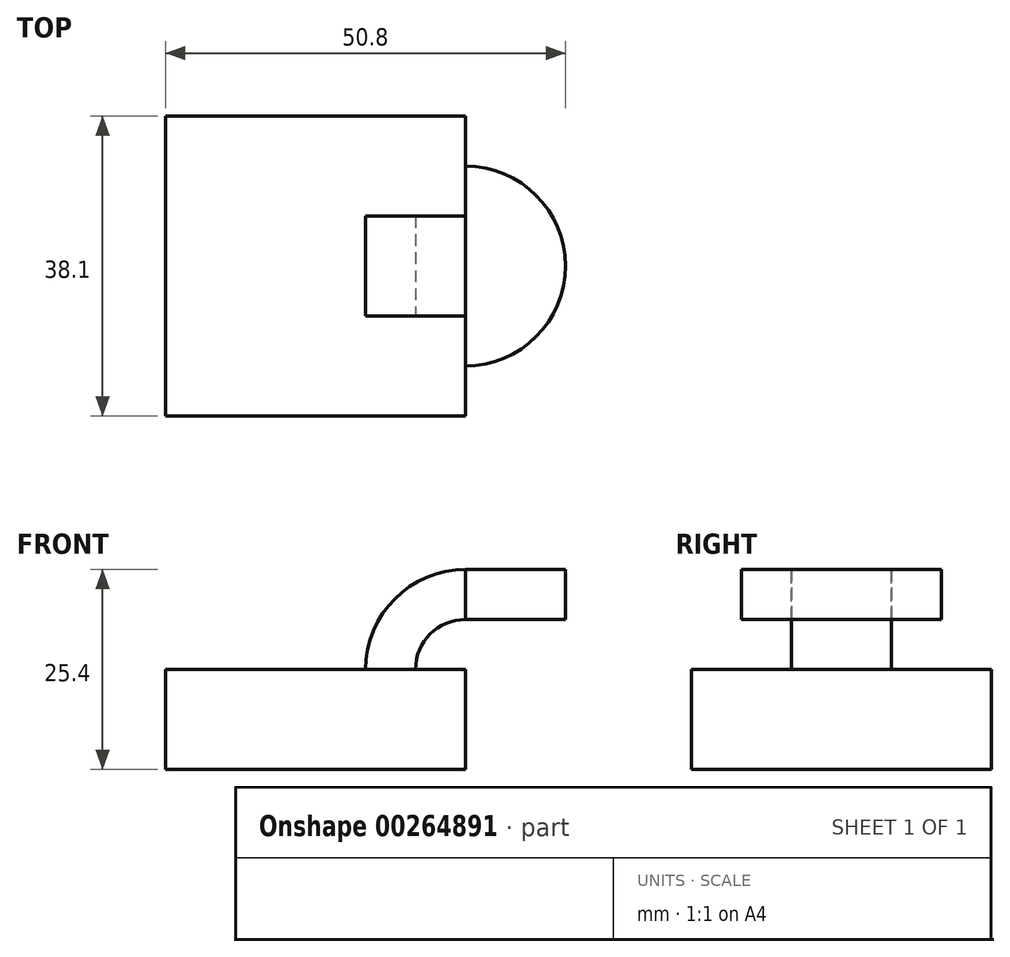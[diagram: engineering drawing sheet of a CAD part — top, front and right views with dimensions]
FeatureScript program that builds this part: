
annotation { "Feature Type Name" : "Feature", "Feature Type Description" : "" }
export const myFeature = defineFeature(function(context is Context, id is Id, definition is map)
    precondition{}
    {
        {
            var Q0;
            Q0=qCreatedBy(makeId("Top.planeOp"),FACE);
            var sketch = newSketch(context, id + "F0", { "sketchPlane" : qUnion([Q0])});
            skLineSegment(sketch, "E0", {"start": v(0, 0) * mm, "end": v(38.1, 0) * mm});
            skLineSegment(sketch, "E1", {"start": v(38.1, 0) * mm, "end": v(38.1, 38.1) * mm});
            skLineSegment(sketch, "E2", {"start": v(38.1, 38.1) * mm, "end": v(0, 38.1) * mm});
            skLineSegment(sketch, "E3", {"start": v(0, 38.1) * mm, "end": v(0, 0) * mm});
            skSolve(sketch);
        }
        {
            var Q0;
            Q0=makeQuery(id+"F0.imprint","IMPRINT",FACE,{"disambiguationData":[TD([[makeQuery(id+"F0.imprint","IMPRINT",EDGE,{"derivedFrom":sQuery(id+"F0.wireOp",EDGE,"E0")}),1.0]])]});
            extrude(context, id + "F1", {"entities" : qUnion([Q0]), "depth" : 12.7 * mm});
        }
        {
            var Q0;
            Q0=qCreatedBy(makeId("Front.planeOp"),FACE);
            cPlane(context, id + "F2", {"entities" : qUnion([Q0]), "cplaneType" : CPlaneType.OFFSET, "offset" : 19.05 * mm, "oppositeDirection" : true, "width" : 152.4 * mm, "height" : 152.4 * mm});
        }
        {
            var Q0;
            Q0=qCreatedBy(id+"F2.planeOp",FACE);
            var sketch = newSketch(context, id + "F3", { "sketchPlane" : qUnion([Q0])});
            skArc(sketch, "E4", {"start": v(38.1, 19.05) * mm, "mid": v(33.6, 17.2) * mm, "end": v(31.75, 12.7) * mm});
            skArc(sketch, "E5.0", {"start": v(38.1, 25.4) * mm, "mid": v(29.12, 21.68) * mm, "end": v(25.4, 12.7) * mm});
            skLineSegment(sketch, "E6", {"start": v(38.1, 19.05) * mm, "end": v(38.1, 25.4) * mm});
            skLineSegment(sketch, "E7", {"start": v(31.75, 12.7) * mm, "end": v(25.4, 12.7) * mm});
            skSolve(sketch);
        }
        {
            var Q0;
            Q0=makeQuery(id+"F3.imprint","IMPRINT",FACE,{"disambiguationData":[TD([[makeQuery(id+"F3.imprint","IMPRINT",EDGE,{"derivedFrom":sQuery(id+"F3.wireOp",EDGE,"E4")}),-1.0]])]});
            var Q1;
            Q1=sQuery(id+"F3.wireOp",EDGE,"E5.0");
            var Q2;
            Q2=makeQuery(id+"F1.opExtrude","SWEPT_FACE",FACE,{"disambiguationData":[OSD([sQuery(id+"F0.wireOp",EDGE,"E2")])]});
            extrude(context, id + "F4", {"entities" : qUnion([Q0]), "surfaceEntities" : qUnion([Q1]), "oppositeDirection" : true, "endBoundEntityFace" : qUnion([Q2]), "depth" : 6.35 * mm, "hasSecondDirection" : true, "secondDirectionOppositeDirection" : false, "secondDirectionDepth" : 6.35 * mm});
        }
        {
            var Q0;
            Q0=qCreatedBy(id+"F2.planeOp",FACE);
            var sketch = newSketch(context, id + "F5", { "sketchPlane" : qUnion([Q0])});
            skLineSegment(sketch, "E8", {"start": v(38.1, 19.05) * mm, "end": v(50.8, 19.05) * mm});
            skLineSegment(sketch, "E9", {"start": v(50.8, 19.05) * mm, "end": v(50.8, 25.4) * mm});
            skLineSegment(sketch, "E10", {"start": v(50.8, 25.4) * mm, "end": v(38.1, 25.4) * mm});
            skLineSegment(sketch, "E11", {"start": v(38.1, 25.4) * mm, "end": v(38.1, 19.05) * mm, "construction": true});
            skLineSegment(sketch, "E12", {"start": v(38.1, 25.4) * mm, "end": v(38.1, 19.05) * mm});
            skSolve(sketch);
        }
        {
            var Q0;
            Q0 = qSketchRegion(id + "F5", true);
            var Q1;
            Q1=sQuery(id+"F5.wireOp",EDGE,"E11");
            revolve(context, id + "F6", {"entities" : qUnion([Q0]), "axis" : qUnion([Q1]), "revolveType" : RevolveType.SYMMETRIC, "angle" : 180 * degree});
        }
    });
